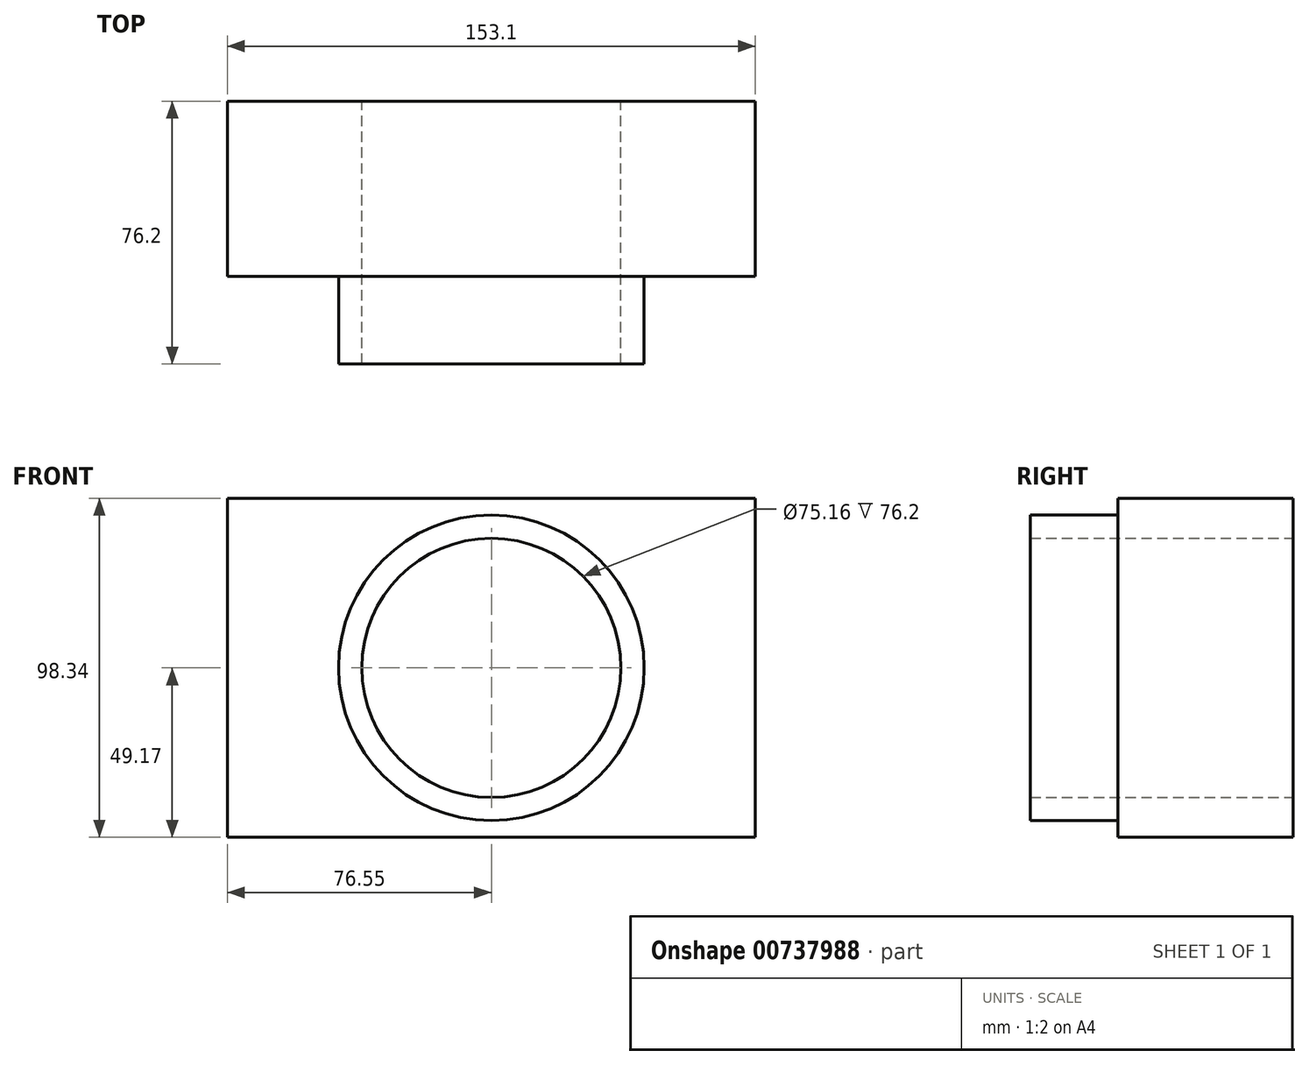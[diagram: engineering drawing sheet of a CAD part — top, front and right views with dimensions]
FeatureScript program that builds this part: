
annotation { "Feature Type Name" : "Feature", "Feature Type Description" : "" }
export const myFeature = defineFeature(function(context is Context, id is Id, definition is map)
    precondition{}
    {
        {
            var Q0;
            Q0=qCreatedBy(makeId("Front.planeOp"),FACE);
            var sketch = newSketch(context, id + "F0", { "sketchPlane" : qUnion([Q0])});
            skLineSegment(sketch, "E0.bottom", {"start": v(76.55, 49.17) * mm, "end": v(-76.55, 49.17) * mm});
            skLineSegment(sketch, "E0.top", {"start": v(76.55, -49.17) * mm, "end": v(-76.55, -49.17) * mm});
            skLineSegment(sketch, "E0.left", {"start": v(76.55, 49.17) * mm, "end": v(76.55, -49.17) * mm});
            skLineSegment(sketch, "E0.right", {"start": v(-76.55, 49.17) * mm, "end": v(-76.55, -49.17) * mm});
            skPoint(sketch, "E0.middle", {"position": v(0, 0) * mm});
            skSolve(sketch);
        }
        {
            var Q0;
            Q0 = qSketchRegion(id + "F0", true);
            extrude(context, id + "F1", {"entities" : qUnion([Q0]), "depth" : 50.8 * mm, "offsetDistance" : 25.4 * mm});
        }
        {
            var Q0;
            Q0=makeQuery(id+"F1.opExtrude","CAP_FACE",FACE,{"disambiguationData":[OSD([sQuery(id+"F0.wireOp",EDGE,"E0.bottom"),sQuery(id+"F0.wireOp",EDGE,"E0.top"),sQuery(id+"F0.wireOp",EDGE,"E0.left"),sQuery(id+"F0.wireOp",EDGE,"E0.right")])],"isStart":false});
            var sketch = newSketch(context, id + "F2", { "sketchPlane" : qUnion([Q0])});
            skCircle(sketch, "E1", {"center": v(0, 0) * mm, "radius": 44.31 * mm});
            skCircle(sketch, "E2", {"center": v(0, 0) * mm, "radius": 37.58 * mm});
            skSolve(sketch);
        }
        {
            var Q0;
            Q0=makeQuery(id+"F2.imprint","IMPRINT",FACE,{"disambiguationData":[TD([[makeQuery(id+"F2.imprint","IMPRINT",EDGE,{"derivedFrom":sQuery(id+"F2.wireOp",EDGE,"E1")}),1.0]])]});
            var Q1;
            Q1 = qSketchRegion(id + "F2", true);
            extrude(context, id + "F3", {"entities" : qUnion([Q0, Q1]), "operationType" : NewBodyOperationType.ADD, "depth" : 25.4 * mm, "offsetDistance" : 25.4 * mm});
        }
        {
            var Q0;
            Q0=makeQuery(id+"F3.boolean.opBoolean","SPLIT",FACE,{"disambiguationData":[TD([makeQuery(id+"F3.opExtrude","SWEPT_FACE",FACE,{"disambiguationData":[OSD([sQuery(id+"F2.wireOp",EDGE,"E2")])]})])],"derivedFrom":makeQuery(id+"F1.opExtrude","CAP_FACE",FACE,{"disambiguationData":[OSD([sQuery(id+"F0.wireOp",EDGE,"E0.bottom"),sQuery(id+"F0.wireOp",EDGE,"E0.top"),sQuery(id+"F0.wireOp",EDGE,"E0.left"),sQuery(id+"F0.wireOp",EDGE,"E0.right")])],"isStart":false})});
            extrude(context, id + "F4", {"entities" : qUnion([Q0]), "operationType" : NewBodyOperationType.REMOVE, "oppositeDirection" : true, "depth" : 76.2 * mm, "offsetDistance" : 25.4 * mm});
        }
    });
